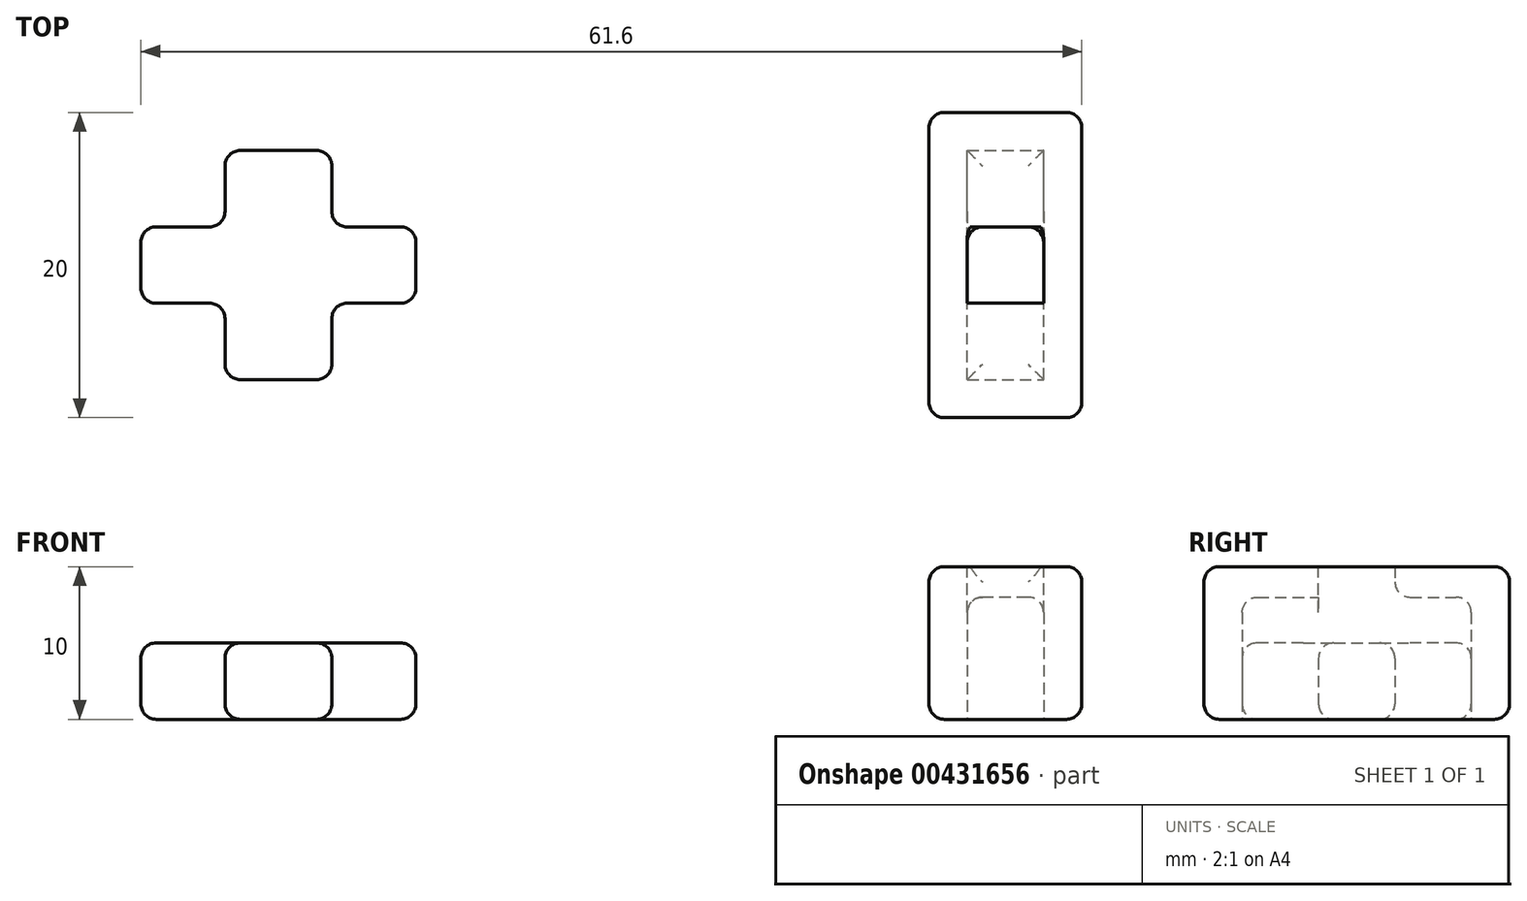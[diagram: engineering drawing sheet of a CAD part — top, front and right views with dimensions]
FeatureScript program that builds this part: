
annotation { "Feature Type Name" : "Feature", "Feature Type Description" : "" }
export const myFeature = defineFeature(function(context is Context, id is Id, definition is map)
    precondition{}
    {
        {
            var Q0;
            Q0=qCreatedBy(makeId("Top.planeOp"),FACE);
            var sketch = newSketch(context, id + "F0", { "sketchPlane" : qUnion([Q0])});
            skLineSegment(sketch, "E0.bottom", {"start": v(5, -10) * mm, "end": v(-5, -10) * mm});
            skLineSegment(sketch, "E0.top", {"start": v(5, 10) * mm, "end": v(-5, 10) * mm});
            skLineSegment(sketch, "E0.left", {"start": v(5, -10) * mm, "end": v(5, 10) * mm});
            skLineSegment(sketch, "E0.right", {"start": v(-5, -10) * mm, "end": v(-5, 10) * mm});
            skPoint(sketch, "E0.middle", {"position": v(0, 0) * mm});
            skSolve(sketch);
        }
        {
            var Q0;
            Q0=makeQuery(id+"F0.imprint","IMPRINT",FACE,{"disambiguationData":[TD([[makeQuery(id+"F0.imprint","IMPRINT",EDGE,{"derivedFrom":sQuery(id+"F0.wireOp",EDGE,"E0.bottom")}),-1.0]])]});
            extrude(context, id + "F1", {"entities" : qUnion([Q0]), "depth" : 10 * mm});
        }
        {
            var Q0;
            Q0=makeQuery(id+"F1.opExtrude","CAP_FACE",FACE,{"disambiguationData":[OSD([sQuery(id+"F0.wireOp",EDGE,"E0.bottom"),sQuery(id+"F0.wireOp",EDGE,"E0.top"),sQuery(id+"F0.wireOp",EDGE,"E0.left"),sQuery(id+"F0.wireOp",EDGE,"E0.right")])],"isStart":true});
            var sketch = newSketch(context, id + "F2", { "sketchPlane" : qUnion([Q0])});
            skLineSegment(sketch, "E1.bottom", {"start": v(-2.5, 7.5) * mm, "end": v(2.5, 7.5) * mm});
            skLineSegment(sketch, "E1.top", {"start": v(-2.5, -7.5) * mm, "end": v(2.5, -7.5) * mm});
            skLineSegment(sketch, "E1.left", {"start": v(-2.5, 7.5) * mm, "end": v(-2.5, -7.5) * mm});
            skLineSegment(sketch, "E1.right", {"start": v(2.5, 7.5) * mm, "end": v(2.5, -7.5) * mm});
            skPoint(sketch, "E1.middle", {"position": v(0, 0) * mm});
            skSolve(sketch);
        }
        {
            var Q0;
            Q0 = qSketchRegion(id + "F2", true);
            extrude(context, id + "F3", {"entities" : qUnion([Q0]), "operationType" : NewBodyOperationType.REMOVE, "oppositeDirection" : true, "depth" : 8 * mm});
        }
        {
            var Q0;
            Q0=makeQuery(id+"F1.opExtrude","CAP_FACE",FACE,{"disambiguationData":[OSD([sQuery(id+"F0.wireOp",EDGE,"E0.bottom"),sQuery(id+"F0.wireOp",EDGE,"E0.top"),sQuery(id+"F0.wireOp",EDGE,"E0.left"),sQuery(id+"F0.wireOp",EDGE,"E0.right")])],"isStart":false});
            var sketch = newSketch(context, id + "F4", { "sketchPlane" : qUnion([Q0])});
            skLineSegment(sketch, "E2.bottom", {"start": v(2.5, -2.5) * mm, "end": v(-2.5, -2.5) * mm});
            skLineSegment(sketch, "E2.top", {"start": v(2.5, 2.5) * mm, "end": v(-2.5, 2.5) * mm});
            skLineSegment(sketch, "E2.left", {"start": v(2.5, -2.5) * mm, "end": v(2.5, 2.5) * mm});
            skLineSegment(sketch, "E2.right", {"start": v(-2.5, -2.5) * mm, "end": v(-2.5, 2.5) * mm});
            skPoint(sketch, "E2.middle", {"position": v(0, 0) * mm});
            skSolve(sketch);
        }
        {
            var Q0;
            Q0 = qSketchRegion(id + "F4", true);
            extrude(context, id + "F5", {"entities" : qUnion([Q0]), "operationType" : NewBodyOperationType.REMOVE, "endBound" : BoundingType.UP_TO_NEXT, "oppositeDirection" : true, "depth" : 25 * mm});
        }
        {
            var Q0;
            Q0=qCreatedBy(makeId("Top.planeOp"),FACE);
            var sketch = newSketch(context, id + "F6", { "sketchPlane" : qUnion([Q0])});
            skLineSegment(sketch, "E3.bottom", {"start": v(-38.6, -2.5) * mm, "end": v(-56.6, -2.5) * mm});
            skLineSegment(sketch, "E3.top", {"start": v(-38.6, 2.5) * mm, "end": v(-56.6, 2.5) * mm});
            skLineSegment(sketch, "E3.left", {"start": v(-38.6, -2.5) * mm, "end": v(-38.6, 2.5) * mm});
            skLineSegment(sketch, "E3.right", {"start": v(-56.6, -2.5) * mm, "end": v(-56.6, 2.5) * mm});
            skPoint(sketch, "E3.middle", {"position": v(-47.6, 0) * mm});
            skLineSegment(sketch, "E4.bottom", {"start": v(-44.1, 7.5) * mm, "end": v(-51.1, 7.5) * mm});
            skLineSegment(sketch, "E4.top", {"start": v(-44.1, -7.5) * mm, "end": v(-51.1, -7.5) * mm});
            skLineSegment(sketch, "E4.left", {"start": v(-44.1, 7.5) * mm, "end": v(-44.1, -7.5) * mm});
            skLineSegment(sketch, "E4.right", {"start": v(-51.1, 7.5) * mm, "end": v(-51.1, -7.5) * mm});
            skSolve(sketch);
        }
        {
            var Q0;
            Q0 = qSketchRegion(id + "F6", true);
            extrude(context, id + "F7", {"entities" : qUnion([Q0]), "depth" : 5 * mm});
        }
        {
            var Q0;
            Q0=makeQuery(id+"F7.opExtrude","CAP_EDGE",EDGE,{"disambiguationData":[OSD([sQuery(id+"F6.wireOp",EDGE,"E4.top")])],"isStart":false});
            var Q1;
            {var subQ0=sQuery(id+"F6.wireOp",EDGE,"E4.left");Q1=makeQuery(id+"F7.opExtrude","CAP_EDGE",EDGE,{"disambiguationData":[OSD([subQ0]),TDD([makeQuery(id+"F6.imprint","IMPRINT",EDGE,{"disambiguationData":[TD([[makeQuery(id+"F6.imprint","INTERSECT",VERTEX,{"derivedFrom":[sQuery(id+"F6.wireOp",EDGE,"E4.top"),subQ0]}),1.0]])],"derivedFrom":subQ0})])],"isStart":false});}
            var Q2;
            {var subQ0=sQuery(id+"F6.wireOp",EDGE,"E3.bottom");Q2=makeQuery(id+"F7.opExtrude","CAP_EDGE",EDGE,{"disambiguationData":[OSD([subQ0]),TDD([makeQuery(id+"F6.imprint","IMPRINT",EDGE,{"disambiguationData":[TD([[makeQuery(id+"F6.imprint","INTERSECT",VERTEX,{"derivedFrom":[subQ0,sQuery(id+"F6.wireOp",EDGE,"E3.left")]}),-1.0]])],"derivedFrom":subQ0})])],"isStart":false});}
            var Q3;
            Q3=makeQuery(id+"F7.opExtrude","CAP_EDGE",EDGE,{"disambiguationData":[OSD([sQuery(id+"F6.wireOp",EDGE,"E3.left")])],"isStart":false});
            var Q4;
            {var subQ0=sQuery(id+"F6.wireOp",EDGE,"E3.top");Q4=makeQuery(id+"F7.opExtrude","CAP_EDGE",EDGE,{"disambiguationData":[OSD([subQ0]),TDD([makeQuery(id+"F6.imprint","IMPRINT",EDGE,{"disambiguationData":[TD([[makeQuery(id+"F6.imprint","INTERSECT",VERTEX,{"derivedFrom":[subQ0,sQuery(id+"F6.wireOp",EDGE,"E3.left")]}),-1.0]])],"derivedFrom":subQ0})])],"isStart":false});}
            var Q5;
            {var subQ0=sQuery(id+"F6.wireOp",EDGE,"E4.left");Q5=makeQuery(id+"F7.opExtrude","CAP_EDGE",EDGE,{"disambiguationData":[OSD([subQ0]),TDD([makeQuery(id+"F6.imprint","IMPRINT",EDGE,{"disambiguationData":[TD([[makeQuery(id+"F6.imprint","INTERSECT",VERTEX,{"derivedFrom":[sQuery(id+"F6.wireOp",EDGE,"E4.bottom"),subQ0]}),-1.0]])],"derivedFrom":subQ0})])],"isStart":false});}
            var Q6;
            Q6=makeQuery(id+"F7.opExtrude","CAP_EDGE",EDGE,{"disambiguationData":[OSD([sQuery(id+"F6.wireOp",EDGE,"E4.bottom")])],"isStart":false});
            var Q7;
            {var subQ0=sQuery(id+"F6.wireOp",EDGE,"E4.right");Q7=makeQuery(id+"F7.opExtrude","CAP_EDGE",EDGE,{"disambiguationData":[OSD([subQ0]),TDD([makeQuery(id+"F6.imprint","IMPRINT",EDGE,{"disambiguationData":[TD([[makeQuery(id+"F6.imprint","INTERSECT",VERTEX,{"derivedFrom":[sQuery(id+"F6.wireOp",EDGE,"E4.bottom"),subQ0]}),-1.0]])],"derivedFrom":subQ0})])],"isStart":false});}
            var Q8;
            {var subQ0=sQuery(id+"F6.wireOp",EDGE,"E3.top");Q8=makeQuery(id+"F7.opExtrude","CAP_EDGE",EDGE,{"disambiguationData":[OSD([subQ0]),TDD([makeQuery(id+"F6.imprint","IMPRINT",EDGE,{"disambiguationData":[TD([[makeQuery(id+"F6.imprint","INTERSECT",VERTEX,{"derivedFrom":[subQ0,sQuery(id+"F6.wireOp",EDGE,"E3.right")]}),1.0]])],"derivedFrom":subQ0})])],"isStart":false});}
            var Q9;
            Q9=makeQuery(id+"F7.opExtrude","CAP_EDGE",EDGE,{"disambiguationData":[OSD([sQuery(id+"F6.wireOp",EDGE,"E3.right")])],"isStart":false});
            var Q10;
            {var subQ0=sQuery(id+"F6.wireOp",EDGE,"E3.bottom");Q10=makeQuery(id+"F7.opExtrude","CAP_EDGE",EDGE,{"disambiguationData":[OSD([subQ0]),TDD([makeQuery(id+"F6.imprint","IMPRINT",EDGE,{"disambiguationData":[TD([[makeQuery(id+"F6.imprint","INTERSECT",VERTEX,{"derivedFrom":[subQ0,sQuery(id+"F6.wireOp",EDGE,"E3.right")]}),1.0]])],"derivedFrom":subQ0})])],"isStart":false});}
            var Q11;
            {var subQ0=sQuery(id+"F6.wireOp",EDGE,"E4.right");Q11=makeQuery(id+"F7.opExtrude","CAP_EDGE",EDGE,{"disambiguationData":[OSD([subQ0]),TDD([makeQuery(id+"F6.imprint","IMPRINT",EDGE,{"disambiguationData":[TD([[makeQuery(id+"F6.imprint","INTERSECT",VERTEX,{"derivedFrom":[sQuery(id+"F6.wireOp",EDGE,"E4.top"),subQ0]}),1.0]])],"derivedFrom":subQ0})])],"isStart":false});}
            var Q12;
            Q12=makeQuery(id+"F7.opExtrude","SWEPT_EDGE",EDGE,{"disambiguationData":[OSD([sQuery(id+"F6.wireOp",EDGE,"E4.top"),sQuery(id+"F6.wireOp",EDGE,"E4.left")])]});
            var Q13;
            Q13=makeQuery(id+"F7.opExtrude","SWEPT_EDGE",EDGE,{"disambiguationData":[OSD([sQuery(id+"F6.wireOp",EDGE,"E4.top"),sQuery(id+"F6.wireOp",EDGE,"E4.right")])]});
            var Q14;
            Q14=makeQuery(id+"F7.opExtrude","SWEPT_EDGE",EDGE,{"disambiguationData":[OSD([sQuery(id+"F6.wireOp",EDGE,"E3.bottom"),sQuery(id+"F6.wireOp",EDGE,"E3.left")])]});
            var Q15;
            Q15=makeQuery(id+"F7.opExtrude","SWEPT_EDGE",EDGE,{"disambiguationData":[OSD([sQuery(id+"F6.wireOp",EDGE,"E3.top"),sQuery(id+"F6.wireOp",EDGE,"E3.left")])]});
            var Q16;
            Q16=makeQuery(id+"F7.opExtrude","SWEPT_EDGE",EDGE,{"disambiguationData":[OSD([sQuery(id+"F6.wireOp",EDGE,"E3.bottom"),sQuery(id+"F6.wireOp",EDGE,"E3.right")])]});
            var Q17;
            Q17=makeQuery(id+"F7.opExtrude","SWEPT_EDGE",EDGE,{"disambiguationData":[OSD([sQuery(id+"F6.wireOp",EDGE,"E3.top"),sQuery(id+"F6.wireOp",EDGE,"E3.right")])]});
            var Q18;
            Q18=makeQuery(id+"F7.opExtrude","SWEPT_EDGE",EDGE,{"disambiguationData":[OSD([sQuery(id+"F6.wireOp",EDGE,"E4.bottom"),sQuery(id+"F6.wireOp",EDGE,"E4.left")])]});
            var Q19;
            Q19=makeQuery(id+"F7.opExtrude","SWEPT_EDGE",EDGE,{"disambiguationData":[OSD([sQuery(id+"F6.wireOp",EDGE,"E4.bottom"),sQuery(id+"F6.wireOp",EDGE,"E4.right")])]});
            var Q20;
            {var subQ0=sQuery(id+"F6.wireOp",EDGE,"E3.top");Q20=makeQuery(id+"F7.opExtrude","CAP_EDGE",EDGE,{"disambiguationData":[OSD([subQ0]),TDD([makeQuery(id+"F6.imprint","IMPRINT",EDGE,{"disambiguationData":[TD([[makeQuery(id+"F6.imprint","INTERSECT",VERTEX,{"derivedFrom":[subQ0,sQuery(id+"F6.wireOp",EDGE,"E3.left")]}),-1.0]])],"derivedFrom":subQ0})])],"isStart":true});}
            var Q21;
            {var subQ0=sQuery(id+"F6.wireOp",EDGE,"E4.left");Q21=makeQuery(id+"F7.opExtrude","CAP_EDGE",EDGE,{"disambiguationData":[OSD([subQ0]),TDD([makeQuery(id+"F6.imprint","IMPRINT",EDGE,{"disambiguationData":[TD([[makeQuery(id+"F6.imprint","INTERSECT",VERTEX,{"derivedFrom":[sQuery(id+"F6.wireOp",EDGE,"E4.bottom"),subQ0]}),-1.0]])],"derivedFrom":subQ0})])],"isStart":true});}
            var Q22;
            {var subQ0=sQuery(id+"F6.wireOp",EDGE,"E3.bottom");Q22=makeQuery(id+"F7.opExtrude","CAP_EDGE",EDGE,{"disambiguationData":[OSD([subQ0]),TDD([makeQuery(id+"F6.imprint","IMPRINT",EDGE,{"disambiguationData":[TD([[makeQuery(id+"F6.imprint","INTERSECT",VERTEX,{"derivedFrom":[subQ0,sQuery(id+"F6.wireOp",EDGE,"E3.left")]}),-1.0]])],"derivedFrom":subQ0})])],"isStart":true});}
            var Q23;
            {var subQ0=sQuery(id+"F6.wireOp",EDGE,"E4.left");Q23=makeQuery(id+"F7.opExtrude","CAP_EDGE",EDGE,{"disambiguationData":[OSD([subQ0]),TDD([makeQuery(id+"F6.imprint","IMPRINT",EDGE,{"disambiguationData":[TD([[makeQuery(id+"F6.imprint","INTERSECT",VERTEX,{"derivedFrom":[sQuery(id+"F6.wireOp",EDGE,"E4.top"),subQ0]}),1.0]])],"derivedFrom":subQ0})])],"isStart":true});}
            var Q24;
            Q24=makeQuery(id+"F7.opExtrude","CAP_EDGE",EDGE,{"disambiguationData":[OSD([sQuery(id+"F6.wireOp",EDGE,"E3.left")])],"isStart":true});
            var Q25;
            Q25=makeQuery(id+"F7.opExtrude","CAP_EDGE",EDGE,{"disambiguationData":[OSD([sQuery(id+"F6.wireOp",EDGE,"E4.bottom")])],"isStart":true});
            var Q26;
            {var subQ0=sQuery(id+"F6.wireOp",EDGE,"E4.right");Q26=makeQuery(id+"F7.opExtrude","CAP_EDGE",EDGE,{"disambiguationData":[OSD([subQ0]),TDD([makeQuery(id+"F6.imprint","IMPRINT",EDGE,{"disambiguationData":[TD([[makeQuery(id+"F6.imprint","INTERSECT",VERTEX,{"derivedFrom":[sQuery(id+"F6.wireOp",EDGE,"E4.bottom"),subQ0]}),-1.0]])],"derivedFrom":subQ0})])],"isStart":true});}
            var Q27;
            {var subQ0=sQuery(id+"F6.wireOp",EDGE,"E3.top");Q27=makeQuery(id+"F7.opExtrude","CAP_EDGE",EDGE,{"disambiguationData":[OSD([subQ0]),TDD([makeQuery(id+"F6.imprint","IMPRINT",EDGE,{"disambiguationData":[TD([[makeQuery(id+"F6.imprint","INTERSECT",VERTEX,{"derivedFrom":[subQ0,sQuery(id+"F6.wireOp",EDGE,"E3.right")]}),1.0]])],"derivedFrom":subQ0})])],"isStart":true});}
            var Q28;
            Q28=makeQuery(id+"F7.opExtrude","CAP_EDGE",EDGE,{"disambiguationData":[OSD([sQuery(id+"F6.wireOp",EDGE,"E3.right")])],"isStart":true});
            var Q29;
            {var subQ0=sQuery(id+"F6.wireOp",EDGE,"E3.bottom");Q29=makeQuery(id+"F7.opExtrude","CAP_EDGE",EDGE,{"disambiguationData":[OSD([subQ0]),TDD([makeQuery(id+"F6.imprint","IMPRINT",EDGE,{"disambiguationData":[TD([[makeQuery(id+"F6.imprint","INTERSECT",VERTEX,{"derivedFrom":[subQ0,sQuery(id+"F6.wireOp",EDGE,"E3.right")]}),1.0]])],"derivedFrom":subQ0})])],"isStart":true});}
            var Q30;
            {var subQ0=sQuery(id+"F6.wireOp",EDGE,"E4.right");Q30=makeQuery(id+"F7.opExtrude","CAP_EDGE",EDGE,{"disambiguationData":[OSD([subQ0]),TDD([makeQuery(id+"F6.imprint","IMPRINT",EDGE,{"disambiguationData":[TD([[makeQuery(id+"F6.imprint","INTERSECT",VERTEX,{"derivedFrom":[sQuery(id+"F6.wireOp",EDGE,"E4.top"),subQ0]}),1.0]])],"derivedFrom":subQ0})])],"isStart":true});}
            var Q31;
            Q31=makeQuery(id+"F7.opExtrude","CAP_EDGE",EDGE,{"disambiguationData":[OSD([sQuery(id+"F6.wireOp",EDGE,"E4.top")])],"isStart":true});
            var Q32;
            Q32=makeQuery(id+"F7.opExtrude","SWEPT_EDGE",EDGE,{"disambiguationData":[OSD([sQuery(id+"F6.wireOp",EDGE,"E3.bottom"),sQuery(id+"F6.wireOp",EDGE,"E4.right")])]});
            var Q33;
            Q33=makeQuery(id+"F7.opExtrude","SWEPT_EDGE",EDGE,{"disambiguationData":[OSD([sQuery(id+"F6.wireOp",EDGE,"E3.bottom"),sQuery(id+"F6.wireOp",EDGE,"E4.left")])]});
            var Q34;
            Q34=makeQuery(id+"F7.opExtrude","SWEPT_EDGE",EDGE,{"disambiguationData":[OSD([sQuery(id+"F6.wireOp",EDGE,"E3.top"),sQuery(id+"F6.wireOp",EDGE,"E4.left")])]});
            var Q35;
            Q35=makeQuery(id+"F7.opExtrude","SWEPT_EDGE",EDGE,{"disambiguationData":[OSD([sQuery(id+"F6.wireOp",EDGE,"E3.top"),sQuery(id+"F6.wireOp",EDGE,"E4.right")])]});
            fillet(context, id + "F8", {"entities" : qUnion([Q0, Q1, Q2, Q3, Q4, Q5, Q6, Q7, Q8, Q9, Q10, Q11, Q12, Q13, Q14, Q15, Q16, Q17, Q18, Q19, Q20, Q21, Q22, Q23, Q24, Q25, Q26, Q27, Q28, Q29, Q30, Q31, Q32, Q33, Q34, Q35]), "radius" : 1 * mm, "tangentPropagation" : true, "allowEdgeOverflow" : false});
        }
        {
            var Q0;
            Q0=makeQuery(id+"F1.opExtrude","CAP_EDGE",EDGE,{"disambiguationData":[OSD([sQuery(id+"F0.wireOp",EDGE,"E0.bottom")])],"isStart":false});
            var Q1;
            Q1=makeQuery(id+"F1.opExtrude","CAP_EDGE",EDGE,{"disambiguationData":[OSD([sQuery(id+"F0.wireOp",EDGE,"E0.right")])],"isStart":false});
            var Q2;
            Q2=makeQuery(id+"F1.opExtrude","CAP_EDGE",EDGE,{"disambiguationData":[OSD([sQuery(id+"F0.wireOp",EDGE,"E0.left")])],"isStart":false});
            var Q3;
            Q3=makeQuery(id+"F5.boolean.opBoolean","COPY",EDGE,{"derivedFrom":makeQuery(id+"F5.opExtrude","CAP_EDGE",EDGE,{"disambiguationData":[OSD([sQuery(id+"F4.wireOp",EDGE,"E2.right")])],"isStart":true})});
            var Q4;
            Q4=makeQuery(id+"F5.boolean.opBoolean","COPY",EDGE,{"derivedFrom":makeQuery(id+"F5.opExtrude","CAP_EDGE",EDGE,{"disambiguationData":[OSD([sQuery(id+"F4.wireOp",EDGE,"E2.top")])],"isStart":true})});
            var Q5;
            Q5=makeQuery(id+"F5.boolean.opBoolean","COPY",EDGE,{"derivedFrom":makeQuery(id+"F5.opExtrude","CAP_EDGE",EDGE,{"disambiguationData":[OSD([sQuery(id+"F4.wireOp",EDGE,"E2.left")])],"isStart":true})});
            var Q6;
            Q6=makeQuery(id+"F5.boolean.opBoolean","COPY",EDGE,{"derivedFrom":makeQuery(id+"F5.opExtrude","CAP_EDGE",EDGE,{"disambiguationData":[OSD([sQuery(id+"F4.wireOp",EDGE,"E2.bottom")])],"isStart":true})});
            var Q7;
            Q7=makeQuery(id+"F1.opExtrude","CAP_EDGE",EDGE,{"disambiguationData":[OSD([sQuery(id+"F0.wireOp",EDGE,"E0.bottom")])],"isStart":true});
            var Q8;
            Q8=makeQuery(id+"F1.opExtrude","SWEPT_EDGE",EDGE,{"disambiguationData":[OSD([sQuery(id+"F0.wireOp",EDGE,"E0.bottom"),sQuery(id+"F0.wireOp",EDGE,"E0.right")])]});
            var Q9;
            Q9=makeQuery(id+"F1.opExtrude","SWEPT_EDGE",EDGE,{"disambiguationData":[OSD([sQuery(id+"F0.wireOp",EDGE,"E0.bottom"),sQuery(id+"F0.wireOp",EDGE,"E0.left")])]});
            var Q10;
            Q10=makeQuery(id+"F1.opExtrude","SWEPT_EDGE",EDGE,{"disambiguationData":[OSD([sQuery(id+"F0.wireOp",EDGE,"E0.top"),sQuery(id+"F0.wireOp",EDGE,"E0.left")])]});
            var Q11;
            Q11=makeQuery(id+"F1.opExtrude","SWEPT_EDGE",EDGE,{"disambiguationData":[OSD([sQuery(id+"F0.wireOp",EDGE,"E0.top"),sQuery(id+"F0.wireOp",EDGE,"E0.right")])]});
            var Q12;
            Q12=makeQuery(id+"F1.opExtrude","CAP_EDGE",EDGE,{"disambiguationData":[OSD([sQuery(id+"F0.wireOp",EDGE,"E0.top")])],"isStart":false});
            var Q13;
            Q13=makeQuery(id+"F1.opExtrude","CAP_EDGE",EDGE,{"disambiguationData":[OSD([sQuery(id+"F0.wireOp",EDGE,"E0.left")])],"isStart":true});
            var Q14;
            Q14=makeQuery(id+"F1.opExtrude","CAP_EDGE",EDGE,{"disambiguationData":[OSD([sQuery(id+"F0.wireOp",EDGE,"E0.right")])],"isStart":true});
            var Q15;
            Q15=makeQuery(id+"F3.boolean.opBoolean","COPY",EDGE,{"derivedFrom":makeQuery(id+"F3.opExtrude","CAP_EDGE",EDGE,{"disambiguationData":[OSD([sQuery(id+"F2.wireOp",EDGE,"E1.left")])],"isStart":true})});
            var Q16;
            Q16=makeQuery(id+"F3.boolean.opBoolean","COPY",EDGE,{"derivedFrom":makeQuery(id+"F3.opExtrude","CAP_EDGE",EDGE,{"disambiguationData":[OSD([sQuery(id+"F2.wireOp",EDGE,"E1.right")])],"isStart":true})});
            var Q17;
            Q17=makeQuery(id+"F3.boolean.opBoolean","COPY",EDGE,{"derivedFrom":makeQuery(id+"F3.opExtrude","CAP_EDGE",EDGE,{"disambiguationData":[OSD([sQuery(id+"F2.wireOp",EDGE,"E1.top")])],"isStart":true})});
            var Q18;
            Q18=makeQuery(id+"F3.boolean.opBoolean","COPY",EDGE,{"derivedFrom":makeQuery(id+"F3.opExtrude","CAP_EDGE",EDGE,{"disambiguationData":[OSD([sQuery(id+"F2.wireOp",EDGE,"E1.bottom")])],"isStart":true})});
            var Q19;
            Q19=makeQuery(id+"F5.boolean.opBoolean","COPY",EDGE,{"derivedFrom":makeQuery(id+"F5.opExtrude","CAP_EDGE",EDGE,{"disambiguationData":[OSD([sQuery(id+"F4.wireOp",EDGE,"E2.top")])],"isStart":false})});
            var Q20;
            Q20=makeQuery(id+"F5.boolean.opBoolean","COPY",EDGE,{"derivedFrom":makeQuery(id+"F5.opExtrude","CAP_EDGE",EDGE,{"disambiguationData":[OSD([sQuery(id+"F4.wireOp",EDGE,"E2.bottom")])],"isStart":false})});
            var Q21;
            Q21=makeQuery(id+"F3.boolean.opBoolean","COPY",EDGE,{"derivedFrom":makeQuery(id+"F3.opExtrude","CAP_EDGE",EDGE,{"disambiguationData":[OSD([sQuery(id+"F2.wireOp",EDGE,"E1.bottom")])],"isStart":false})});
            var Q22;
            {var subQ0=sQuery(id+"F2.wireOp",EDGE,"E1.left");var subQ1=sQuery(id+"F2.wireOp",EDGE,"E1.bottom");Q22=makeQuery(id+"F5.boolean.opBoolean","SPLIT",EDGE,{"disambiguationData":[TD([makeQuery(id+"F3.boolean.opBoolean","COPY",FACE,{"derivedFrom":makeQuery(id+"F3.opExtrude","SWEPT_FACE",FACE,{"disambiguationData":[OSD([subQ1])]})})])],"derivedFrom":makeQuery(id+"F3.boolean.opBoolean","COPY",EDGE,{"derivedFrom":makeQuery(id+"F3.opExtrude","CAP_EDGE",EDGE,{"disambiguationData":[OSD([subQ0])],"isStart":false})})});}
            var Q23;
            {var subQ0=sQuery(id+"F2.wireOp",EDGE,"E1.right");var subQ1=sQuery(id+"F2.wireOp",EDGE,"E1.top");Q23=makeQuery(id+"F5.boolean.opBoolean","SPLIT",EDGE,{"disambiguationData":[TD([makeQuery(id+"F3.boolean.opBoolean","COPY",FACE,{"derivedFrom":makeQuery(id+"F3.opExtrude","SWEPT_FACE",FACE,{"disambiguationData":[OSD([subQ1])]})})])],"derivedFrom":makeQuery(id+"F3.boolean.opBoolean","COPY",EDGE,{"derivedFrom":makeQuery(id+"F3.opExtrude","CAP_EDGE",EDGE,{"disambiguationData":[OSD([subQ0])],"isStart":false})})});}
            var Q24;
            Q24=makeQuery(id+"F3.boolean.opBoolean","COPY",EDGE,{"derivedFrom":makeQuery(id+"F3.opExtrude","CAP_EDGE",EDGE,{"disambiguationData":[OSD([sQuery(id+"F2.wireOp",EDGE,"E1.top")])],"isStart":false})});
            var Q25;
            {var subQ0=sQuery(id+"F2.wireOp",EDGE,"E1.right");var subQ1=sQuery(id+"F2.wireOp",EDGE,"E1.bottom");Q25=makeQuery(id+"F5.boolean.opBoolean","SPLIT",EDGE,{"disambiguationData":[TD([makeQuery(id+"F3.boolean.opBoolean","COPY",FACE,{"derivedFrom":makeQuery(id+"F3.opExtrude","SWEPT_FACE",FACE,{"disambiguationData":[OSD([subQ1])]})})])],"derivedFrom":makeQuery(id+"F3.boolean.opBoolean","COPY",EDGE,{"derivedFrom":makeQuery(id+"F3.opExtrude","CAP_EDGE",EDGE,{"disambiguationData":[OSD([subQ0])],"isStart":false})})});}
            var Q26;
            {var subQ0=sQuery(id+"F2.wireOp",EDGE,"E1.left");var subQ1=sQuery(id+"F2.wireOp",EDGE,"E1.top");Q26=makeQuery(id+"F5.boolean.opBoolean","SPLIT",EDGE,{"disambiguationData":[TD([makeQuery(id+"F3.boolean.opBoolean","COPY",FACE,{"derivedFrom":makeQuery(id+"F3.opExtrude","SWEPT_FACE",FACE,{"disambiguationData":[OSD([subQ1])]})})])],"derivedFrom":makeQuery(id+"F3.boolean.opBoolean","COPY",EDGE,{"derivedFrom":makeQuery(id+"F3.opExtrude","CAP_EDGE",EDGE,{"disambiguationData":[OSD([subQ0])],"isStart":false})})});}
            var Q27;
            Q27=makeQuery(id+"F1.opExtrude","CAP_EDGE",EDGE,{"disambiguationData":[OSD([sQuery(id+"F0.wireOp",EDGE,"E0.top")])],"isStart":true});
            fillet(context, id + "F9", {"entities" : qUnion([Q0, Q1, Q2, Q3, Q4, Q5, Q6, Q7, Q8, Q9, Q10, Q11, Q12, Q13, Q14, Q15, Q16, Q17, Q18, Q19, Q20, Q21, Q22, Q23, Q24, Q25, Q26, Q27]), "radius" : 1 * mm, "tangentPropagation" : true, "allowEdgeOverflow" : false});
        }
    });
